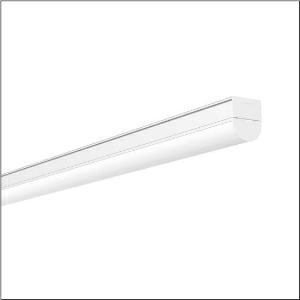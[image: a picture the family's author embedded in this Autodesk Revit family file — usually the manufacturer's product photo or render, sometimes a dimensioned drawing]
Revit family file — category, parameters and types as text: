
# Revit family: ecopack_r__31_51lj12dkm40a_26af
name_source: partatom
category: Lighting Fixtures
units: mm (PartAtom-declared; Revit-internal decimal feet)

## family parameters
Cut with Voids When Loaded = No
Host = Face
Light Source = No
Part Type = Normal
Room Calculation Point = No
Round Connector Dimension = Use Diameter
Shared = No

## types (1)
- --- (1 x LED, 4290 lm, 33 W, 5000K)
    Apparent Load = 33 VA
    CIE Flux Codes = 39 67 87 89 100
    Color Rendering = 80
    Color Temperature = 5000K
    Default Elevation = 1800 mm
    Description = Ecopack® 31, diffuser luminaire, primary optical cover: cover, of PC, frosted, light emission: direct distribution, primary light characteristic: symmetric, installation type: surface-mounted, LED, rated luminous flux: 4.300lm, luminous efficacy: 130lm/W, light colour: 830/840/850, colour temperature: 3000/4000/5000K, control gear: ECG DALI, with terminal, 5-pole, mains connection: 220..240V, AC, 50/60Hz, rated input power: 33W, housing, of aluminium, traffic white (RAL 9016), length: 1.150mm, width: 56mm, height: 68mm, end cap, of PC, white, protection rating (complete): IP20, insulation class (complete): insulation class I (protective earthing), certification: CE, impact resistance: IK06, permissible operating ambient temperature: -20..+40°C, packaging unit: 1 piece
    Height = 68 mm
    Lamp = 1 x LED
    Lamp Light Flux = 4290 lm
    Lamp Power = 33 W
    Lamp count = 1
    Length = 1149 mm
    Luminous efficacy = 130 lm/W
    Manufacturer = Siteco
    ModVariant = No
    Model = 51LJ12DKM40A
    Mounting Place = Ceiling
    Mounting Type = Surface mounted
    Number of Poles = 1
    OnlyDefault = Yes
    Power Factor = 1
    Product Name = Ecopack® 31
    Product group = diffuser luminaire
    ProductGroupID = 304
    Protection Class = Protection class I
    Protection Degree = IP 20
    RLX_Detail_Level = 1
    RLX_Emergency_Light_Flux = 0 lm
    RLX_Emergency_Type = 0
    RLX_Emergency_Type_DB = No
    RlxData = <blob elided: 24993 chars, md5=53eed791>
    Socket = socket
    Standby Power = 0 W
    System Light Flux = 4290 lm
    System Power = 33 W
    Type Comments = individual setting: colour temperature 5000K
    Type Image = l_1007030.jpg
    URL = http://relux.com
    VarID = @adj_124927
    Voltage = 0 V
    Weight = 0.00 kg
    Width = 56 mm

## geometry (parser evidence)
native form markers: Blend x4, Sweep x13
no freeform markers — native parametric forms only
